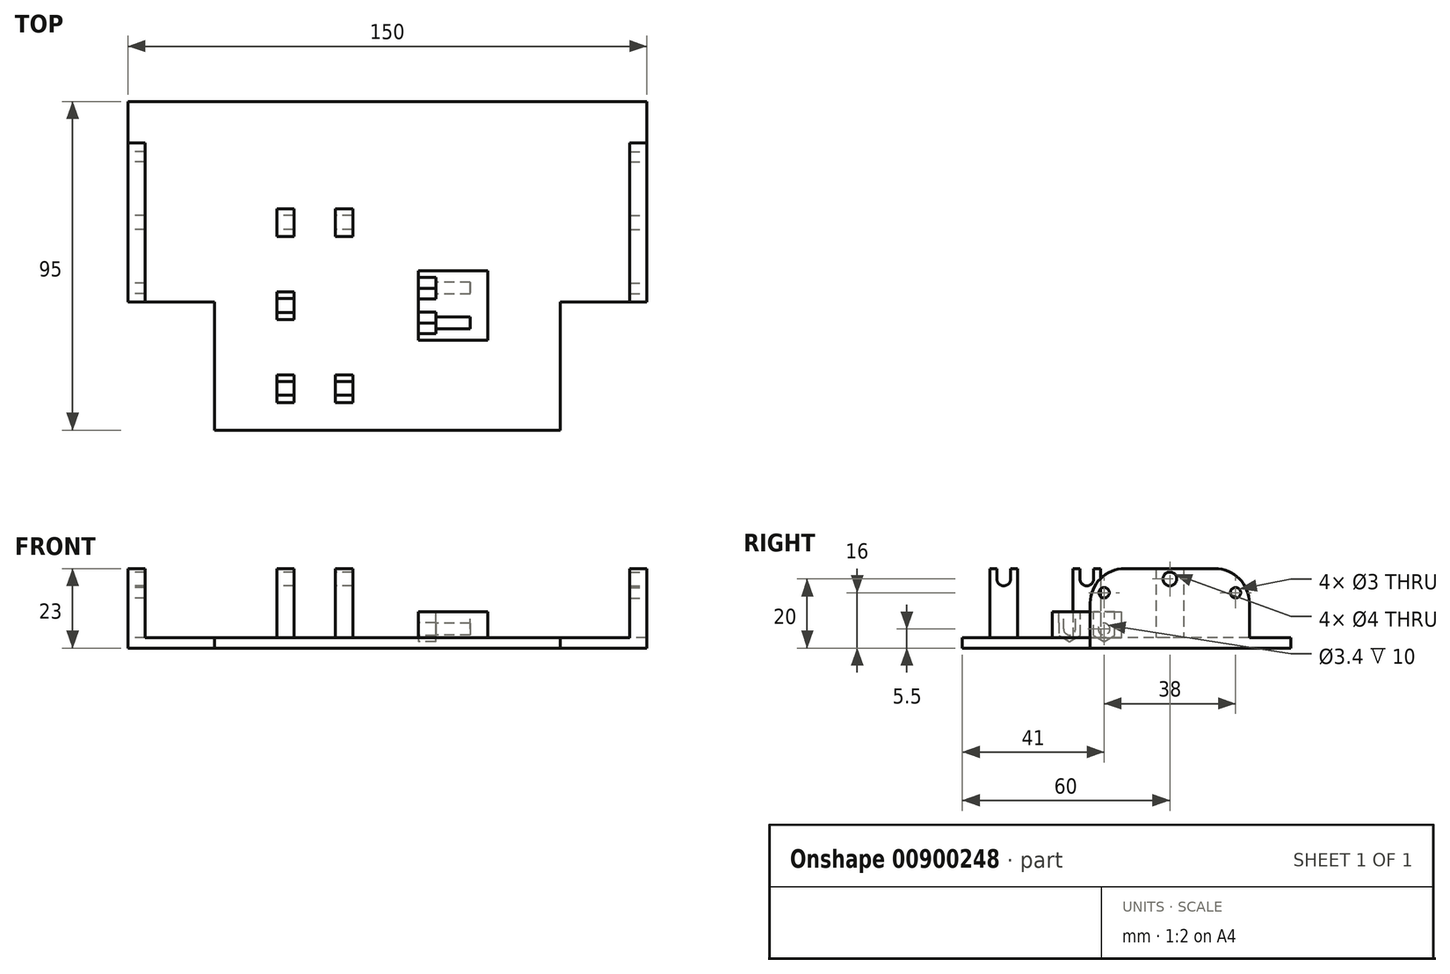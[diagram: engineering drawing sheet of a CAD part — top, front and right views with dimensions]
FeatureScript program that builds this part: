
annotation { "Feature Type Name" : "Feature", "Feature Type Description" : "" }
export const myFeature = defineFeature(function(context is Context, id is Id, definition is map)
    precondition{}
    {
        {
            var Q0;
            Q0=qCreatedBy(makeId("Top.planeOp"),FACE);
            var sketch = newSketch(context, id + "F0", { "sketchPlane" : qUnion([Q0])});
            skLineSegment(sketch, "E0.top", {"start": v(50, -18.5) * mm, "end": v(-50, -18.5) * mm});
            skLineSegment(sketch, "E0.left", {"start": v(50, 18.5) * mm, "end": v(50, -18.5) * mm});
            skLineSegment(sketch, "E0.right", {"start": v(-50, 18.5) * mm, "end": v(-50, -18.5) * mm});
            skPoint(sketch, "E0.middle", {"position": v(0, 0) * mm});
            skLineSegment(sketch, "E1.bottom", {"start": v(-75, 76.5) * mm, "end": v(75, 76.5) * mm});
            skLineSegment(sketch, "E1.top", {"start": v(-75, 18.5) * mm, "end": v(-50, 18.5) * mm});
            skLineSegment(sketch, "E1.left", {"start": v(-75, 76.5) * mm, "end": v(-75, 18.5) * mm});
            skLineSegment(sketch, "E1.right", {"start": v(75, 76.5) * mm, "end": v(75, 18.5) * mm});
            skLineSegment(sketch, "E2.trimOffspring", {"start": v(50, 18.5) * mm, "end": v(75, 18.5) * mm});
            skSolve(sketch);
        }
        {
            var Q0;
            Q0 = qSketchRegion(id + "F0", true);
            extrude(context, id + "F1", {"entities" : qUnion([Q0]), "oppositeDirection" : true, "depth" : 3 * mm, "offsetDistance" : 25.4 * mm});
        }
        {
            var Q0;
            Q0=makeQuery(id+"F1.opExtrude","SWEPT_FACE",FACE,{"disambiguationData":[OSD([sQuery(id+"F0.wireOp",EDGE,"E1.right")])]});
            var sketch = newSketch(context, id + "F2", { "sketchPlane" : qUnion([Q0])});
            skLineSegment(sketch, "E3.bottom", {"start": v(18.5, -3) * mm, "end": v(64.5, -3) * mm});
            skLineSegment(sketch, "E3.top", {"start": v(28.5, 20) * mm, "end": v(54.5, 20) * mm});
            skLineSegment(sketch, "E3.left", {"start": v(18.5, -3) * mm, "end": v(18.5, 10) * mm});
            skLineSegment(sketch, "E3.right", {"start": v(64.5, -3) * mm, "end": v(64.5, 10) * mm});
            skCircle(sketch, "E4", {"center": v(41.5, 17) * mm, "radius": 2 * mm});
            skCircle(sketch, "E5", {"center": v(22.5, 13) * mm, "radius": 1.5 * mm});
            skCircle(sketch, "E6", {"center": v(60.5, 13) * mm, "radius": 1.5 * mm});
            skPoint(sketch, "E7.visualSharp", {"position": v(18.5, 20) * mm});
            skArc(sketch, "E7.filletArc", {"start": v(28.5, 20) * mm, "mid": v(21.43, 17.07) * mm, "end": v(18.5, 10) * mm});
            skPoint(sketch, "E8.visualSharp", {"position": v(64.5, 20) * mm});
            skArc(sketch, "E8.filletArc", {"start": v(64.5, 10) * mm, "mid": v(61.57, 17.07) * mm, "end": v(54.5, 20) * mm});
            skSolve(sketch);
        }
        {
            var Q0;
            Q0 = qSketchRegion(id + "F2", true);
            extrude(context, id + "F3", {"entities" : qUnion([Q0]), "operationType" : NewBodyOperationType.ADD, "oppositeDirection" : true, "depth" : 5 * mm, "offsetDistance" : 25.4 * mm});
        }
        {
            var Q0;
            Q0=makeQuery(id+"F1.opExtrude","SWEPT_FACE",FACE,{"disambiguationData":[OSD([sQuery(id+"F0.wireOp",EDGE,"E1.left")])]});
            var sketch = newSketch(context, id + "F4", { "sketchPlane" : qUnion([Q0])});
            skLineSegment(sketch, "E9.0.0", {"start": v(-64.5, 0) * mm, "end": v(-18.5, 0) * mm});
            skLineSegment(sketch, "E9.0.1", {"start": v(-18.5, 0) * mm, "end": v(-18.5, 10) * mm});
            skArc(sketch, "E9.0.2", {"start": v(-18.5, 10) * mm, "mid": v(-21.43, 17.07) * mm, "end": v(-28.5, 20) * mm});
            skLineSegment(sketch, "E9.0.3", {"start": v(-28.5, 20) * mm, "end": v(-54.5, 20) * mm});
            skArc(sketch, "E9.0.4", {"start": v(-54.5, 20) * mm, "mid": v(-61.57, 17.07) * mm, "end": v(-64.5, 10) * mm});
            skLineSegment(sketch, "E9.0.5", {"start": v(-64.5, 10) * mm, "end": v(-64.5, 0) * mm});
            skCircle(sketch, "E10.0", {"center": v(-60.5, 13) * mm, "radius": 1.5 * mm});
            skCircle(sketch, "E11.0", {"center": v(-41.5, 17) * mm, "radius": 2 * mm});
            skCircle(sketch, "E12.0", {"center": v(-22.5, 13) * mm, "radius": 1.5 * mm});
            skSolve(sketch);
        }
        {
            var Q0;
            Q0 = qSketchRegion(id + "F4", true);
            extrude(context, id + "F5", {"entities" : qUnion([Q0]), "operationType" : NewBodyOperationType.ADD, "oppositeDirection" : true, "depth" : 5 * mm, "offsetDistance" : 25.4 * mm});
        }
        {
            var Q0;
            Q0=makeQuery(id+"F1.opExtrude","CAP_FACE",FACE,{"disambiguationData":[OSD([sQuery(id+"F0.wireOp",EDGE,"E0.top"),sQuery(id+"F0.wireOp",EDGE,"E0.left"),sQuery(id+"F0.wireOp",EDGE,"E0.right"),sQuery(id+"F0.wireOp",EDGE,"E1.bottom"),sQuery(id+"F0.wireOp",EDGE,"E1.top"),sQuery(id+"F0.wireOp",EDGE,"E1.left"),sQuery(id+"F0.wireOp",EDGE,"E1.right"),sQuery(id+"F0.wireOp",EDGE,"E2.trimOffspring")])],"isStart":true});
            var sketch = newSketch(context, id + "F6", { "sketchPlane" : qUnion([Q0])});
            skLineSegment(sketch, "E13.bottom", {"start": v(-32, 45.5) * mm, "end": v(-27, 45.5) * mm});
            skLineSegment(sketch, "E13.top", {"start": v(-32, 37.5) * mm, "end": v(-27, 37.5) * mm});
            skLineSegment(sketch, "E13.left", {"start": v(-32, 45.5) * mm, "end": v(-32, 37.5) * mm});
            skLineSegment(sketch, "E13.right", {"start": v(-27, 45.5) * mm, "end": v(-27, 37.5) * mm});
            skLineSegment(sketch, "E14.bottom", {"start": v(-32, 21.5) * mm, "end": v(-27, 21.5) * mm});
            skLineSegment(sketch, "E14.top", {"start": v(-32, 13.5) * mm, "end": v(-27, 13.5) * mm});
            skLineSegment(sketch, "E14.left", {"start": v(-32, 21.5) * mm, "end": v(-32, 13.5) * mm});
            skLineSegment(sketch, "E14.right", {"start": v(-27, 21.5) * mm, "end": v(-27, 13.5) * mm});
            skLineSegment(sketch, "E15.bottom", {"start": v(-32, -2.5) * mm, "end": v(-27, -2.5) * mm});
            skLineSegment(sketch, "E15.top", {"start": v(-32, -10.5) * mm, "end": v(-27, -10.5) * mm});
            skLineSegment(sketch, "E15.left", {"start": v(-32, -2.5) * mm, "end": v(-32, -10.5) * mm});
            skLineSegment(sketch, "E15.right", {"start": v(-27, -2.5) * mm, "end": v(-27, -10.5) * mm});
            skLineSegment(sketch, "E16.bottom", {"start": v(-15, 45.5) * mm, "end": v(-10, 45.5) * mm});
            skLineSegment(sketch, "E16.top", {"start": v(-15, 37.5) * mm, "end": v(-10, 37.5) * mm});
            skLineSegment(sketch, "E16.left", {"start": v(-15, 45.5) * mm, "end": v(-15, 37.5) * mm});
            skLineSegment(sketch, "E16.right", {"start": v(-10, 45.5) * mm, "end": v(-10, 37.5) * mm});
            skLineSegment(sketch, "E17.bottom", {"start": v(-15, -2.5) * mm, "end": v(-10, -2.5) * mm});
            skLineSegment(sketch, "E17.top", {"start": v(-15, -10.5) * mm, "end": v(-10, -10.5) * mm});
            skLineSegment(sketch, "E17.left", {"start": v(-15, -2.5) * mm, "end": v(-15, -10.5) * mm});
            skLineSegment(sketch, "E17.right", {"start": v(-10, -2.5) * mm, "end": v(-10, -10.5) * mm});
            skSolve(sketch);
        }
        {
            var Q0;
            Q0 = qSketchRegion(id + "F6", true);
            extrude(context, id + "F7", {"entities" : qUnion([Q0]), "operationType" : NewBodyOperationType.ADD, "depth" : 20 * mm, "offsetDistance" : 25.4 * mm});
        }
        {
            var Q0;
            Q0=makeQuery(id+"F7.opExtrude","SWEPT_FACE",FACE,{"disambiguationData":[OSD([sQuery(id+"F6.wireOp",EDGE,"E15.left")])]});
            var sketch = newSketch(context, id + "F8", { "sketchPlane" : qUnion([Q0])});
            skArc(sketch, "E18", {"start": v(4.5, 17) * mm, "mid": v(6.53, 15) * mm, "end": v(8.5, 17.05) * mm});
            skArc(sketch, "E19", {"start": v(-19.5, 17) * mm, "mid": v(-17.5, 15) * mm, "end": v(-15.5, 17) * mm});
            skLineSegment(sketch, "E20", {"start": v(-19.5, 17) * mm, "end": v(-19.5, 20.1) * mm});
            skLineSegment(sketch, "E21", {"start": v(-15.5, 17) * mm, "end": v(-15.5, 20.64) * mm});
            skLineSegment(sketch, "E22", {"start": v(-15.5, 20.64) * mm, "end": v(-19.5, 20.1) * mm});
            skLineSegment(sketch, "E23", {"start": v(4.5, 17) * mm, "end": v(4.48, 22.22) * mm});
            skLineSegment(sketch, "E24", {"start": v(8.5, 17.05) * mm, "end": v(8.37, 22.14) * mm});
            skLineSegment(sketch, "E25", {"start": v(8.37, 22.14) * mm, "end": v(4.48, 22.22) * mm});
            skSolve(sketch);
        }
        {
            var Q0;
            Q0 = qSketchRegion(id + "F8", true);
            extrude(context, id + "F9", {"entities" : qUnion([Q0]), "operationType" : NewBodyOperationType.REMOVE, "oppositeDirection" : true, "depth" : 25.4 * mm, "offsetDistance" : 25.4 * mm});
        }
        {
            var Q0;
            Q0=makeQuery(id+"F7.opExtrude","SWEPT_FACE",FACE,{"disambiguationData":[OSD([sQuery(id+"F6.wireOp",EDGE,"E13.left")])]});
            var sketch = newSketch(context, id + "F10", { "sketchPlane" : qUnion([Q0])});
            skCircle(sketch, "E26.0", {"center": v(-41.5, 17) * mm, "radius": 2 * mm});
            skSolve(sketch);
        }
        {
            var Q0;
            Q0 = qSketchRegion(id + "F10", true);
            extrude(context, id + "F11", {"entities" : qUnion([Q0]), "operationType" : NewBodyOperationType.REMOVE, "oppositeDirection" : true, "depth" : 25.4 * mm, "offsetDistance" : 25.4 * mm});
        }
        {
            var Q0;
            Q0=makeQuery(id+"F1.opExtrude","CAP_FACE",FACE,{"disambiguationData":[OSD([sQuery(id+"F0.wireOp",EDGE,"E0.top"),sQuery(id+"F0.wireOp",EDGE,"E0.left"),sQuery(id+"F0.wireOp",EDGE,"E0.right"),sQuery(id+"F0.wireOp",EDGE,"E1.bottom"),sQuery(id+"F0.wireOp",EDGE,"E1.top"),sQuery(id+"F0.wireOp",EDGE,"E1.left"),sQuery(id+"F0.wireOp",EDGE,"E1.right"),sQuery(id+"F0.wireOp",EDGE,"E2.trimOffspring")])],"isStart":true});
            var sketch = newSketch(context, id + "F12", { "sketchPlane" : qUnion([Q0])});
            skLineSegment(sketch, "E27.bottom", {"start": v(9, 7.5) * mm, "end": v(29, 7.5) * mm});
            skLineSegment(sketch, "E27.top", {"start": v(9, 27.5) * mm, "end": v(29, 27.5) * mm});
            skLineSegment(sketch, "E27.left", {"start": v(9, 7.5) * mm, "end": v(9, 27.5) * mm});
            skLineSegment(sketch, "E27.right", {"start": v(29, 7.5) * mm, "end": v(29, 27.5) * mm});
            skSolve(sketch);
        }
        {
            var Q0;
            Q0=makeQuery(id+"F12.imprint","IMPRINT",FACE,{"disambiguationData":[TD([[makeQuery(id+"F12.imprint","IMPRINT",EDGE,{"derivedFrom":sQuery(id+"F12.wireOp",EDGE,"E27.bottom")}),1.0]])]});
            extrude(context, id + "F13", {"entities" : qUnion([Q0]), "operationType" : NewBodyOperationType.ADD, "depth" : 7.5 * mm, "offsetDistance" : 25 * mm});
        }
        {
            var Q0;
            Q0=makeQuery(id+"F13.opExtrude","SWEPT_FACE",FACE,{"disambiguationData":[OSD([sQuery(id+"F12.wireOp",EDGE,"E27.left")])]});
            var sketch = newSketch(context, id + "F14", { "sketchPlane" : qUnion([Q0])});
            skCircle(sketch, "E28.cCircle", {"center": v(-22.5, 2.5) * mm, "radius": 3.1 * mm, "construction": true});
            skLineSegment(sketch, "E28.0", {"start": v(-19.4, 0.71) * mm, "end": v(-22.5, -1.08) * mm});
            skLineSegment(sketch, "E28.1", {"start": v(-22.5, -1.08) * mm, "end": v(-25.6, 0.71) * mm});
            skLineSegment(sketch, "E28.2", {"start": v(-25.6, 0.71) * mm, "end": v(-25.6, 4.29) * mm});
            skLineSegment(sketch, "E28.3", {"start": v(-25.6, 4.29) * mm, "end": v(-22.5, 6.08) * mm});
            skLineSegment(sketch, "E28.4", {"start": v(-22.5, 6.08) * mm, "end": v(-19.4, 4.29) * mm});
            skLineSegment(sketch, "E28.5", {"start": v(-19.4, 4.29) * mm, "end": v(-19.4, 0.71) * mm});
            skPoint(sketch, "E28.0.midPoint", {"position": v(-20.95, -0.18) * mm});
            skCircle(sketch, "E29.cCircle", {"center": v(-12.5, 2.5) * mm, "radius": 3.1 * mm, "construction": true});
            skPoint(sketch, "E29.cCircle.centerSnap0", {"position": v(-25.6, 2.5) * mm});
            skLineSegment(sketch, "E29.0", {"start": v(-9.4, 0.71) * mm, "end": v(-12.5, -1.08) * mm});
            skLineSegment(sketch, "E29.1", {"start": v(-12.5, -1.08) * mm, "end": v(-15.6, 0.71) * mm});
            skLineSegment(sketch, "E29.2", {"start": v(-15.6, 0.71) * mm, "end": v(-15.6, 4.29) * mm});
            skLineSegment(sketch, "E29.3", {"start": v(-15.6, 4.29) * mm, "end": v(-12.5, 6.08) * mm});
            skLineSegment(sketch, "E29.4", {"start": v(-12.5, 6.08) * mm, "end": v(-9.4, 4.29) * mm});
            skLineSegment(sketch, "E29.5", {"start": v(-9.4, 4.29) * mm, "end": v(-9.4, 0.71) * mm});
            skPoint(sketch, "E29.0.midPoint", {"position": v(-10.95, -0.18) * mm});
            skLineSegment(sketch, "E30", {"start": v(-17.5, -2.38) * mm, "end": v(-17.5, 12.1) * mm, "construction": true});
            skCircle(sketch, "E31", {"center": v(-22.5, 2.5) * mm, "radius": 1.7 * mm});
            skCircle(sketch, "E32", {"center": v(-12.5, 2.5) * mm, "radius": 1.7 * mm});
            skLineSegment(sketch, "E33.bottom", {"start": v(-25.6, 4.29) * mm, "end": v(-19.4, 4.29) * mm});
            skLineSegment(sketch, "E33.top", {"start": v(-25.6, 10.64) * mm, "end": v(-19.4, 10.64) * mm});
            skLineSegment(sketch, "E33.left", {"start": v(-25.6, 4.29) * mm, "end": v(-25.6, 10.64) * mm});
            skLineSegment(sketch, "E33.right", {"start": v(-19.4, 4.29) * mm, "end": v(-19.4, 10.64) * mm});
            skLineSegment(sketch, "E34.bottom", {"start": v(-15.6, 4.29) * mm, "end": v(-9.38, 4.29) * mm});
            skLineSegment(sketch, "E34.top", {"start": v(-15.6, 11.52) * mm, "end": v(-9.38, 11.52) * mm});
            skLineSegment(sketch, "E34.left", {"start": v(-15.6, 4.29) * mm, "end": v(-15.6, 11.52) * mm});
            skLineSegment(sketch, "E35", {"start": v(-9.38, 4.29) * mm, "end": v(-9.38, 11.52) * mm});
            skSolve(sketch);
        }
        {
            var Q0;
            Q0 = qSketchRegion(id + "F14", true);
            var Q1;
            Q1=makeQuery(id+"F14.imprint","IMPRINT",FACE,{"disambiguationData":[TD([[makeQuery(id+"F14.imprint","IMPRINT",EDGE,{"derivedFrom":sQuery(id+"F14.wireOp",EDGE,"E31")}),1.0]])]});
            var Q2;
            Q2=makeQuery(id+"F14.imprint","IMPRINT",FACE,{"disambiguationData":[TD([[makeQuery(id+"F14.imprint","IMPRINT",EDGE,{"derivedFrom":sQuery(id+"F14.wireOp",EDGE,"E32")}),1.0]])]});
            extrude(context, id + "F15", {"entities" : qUnion([Q0, Q1, Q2]), "operationType" : NewBodyOperationType.REMOVE, "oppositeDirection" : true, "depth" : 5 * mm, "offsetDistance" : 25 * mm});
        }
        {
            var Q0;
            Q0=makeQuery(id+"F14.imprint","IMPRINT",FACE,{"disambiguationData":[TD([[makeQuery(id+"F14.imprint","IMPRINT",EDGE,{"derivedFrom":sQuery(id+"F14.wireOp",EDGE,"E31")}),1.0]])]});
            var Q1;
            Q1=makeQuery(id+"F14.imprint","IMPRINT",FACE,{"disambiguationData":[TD([[makeQuery(id+"F14.imprint","IMPRINT",EDGE,{"derivedFrom":sQuery(id+"F14.wireOp",EDGE,"E32")}),1.0]])]});
            extrude(context, id + "F16", {"entities" : qUnion([Q0, Q1]), "operationType" : NewBodyOperationType.REMOVE, "oppositeDirection" : true, "depth" : 15 * mm, "offsetDistance" : 25 * mm});
        }
        {
            var Q0;
            Q0=makeQuery(id+"F15.boolean.opBoolean","COPY",FACE,{"derivedFrom":makeQuery(id+"F15.opExtrude","CAP_FACE",FACE,{"disambiguationData":[OSD([sQuery(id+"F14.wireOp",EDGE,"E29.0"),sQuery(id+"F14.wireOp",EDGE,"E29.1"),sQuery(id+"F14.wireOp",EDGE,"E29.2"),sQuery(id+"F14.wireOp",EDGE,"E29.5"),sQuery(id+"F14.wireOp",EDGE,"E34.bottom"),sQuery(id+"F14.wireOp",EDGE,"E34.top"),sQuery(id+"F14.wireOp",EDGE,"E34.left"),sQuery(id+"F14.wireOp",EDGE,"E35")])],"isStart":false})});
            var sketch = newSketch(context, id + "F17", { "sketchPlane" : qUnion([Q0])});
            skLineSegment(sketch, "E36.bottom", {"start": v(-14.2, 2.5) * mm, "end": v(-10.8, 2.5) * mm});
            skLineSegment(sketch, "E36.top", {"start": v(-14.2, 8.48) * mm, "end": v(-10.8, 8.48) * mm});
            skLineSegment(sketch, "E36.left", {"start": v(-14.2, 2.5) * mm, "end": v(-14.2, 8.48) * mm});
            skLineSegment(sketch, "E36.right", {"start": v(-10.8, 2.5) * mm, "end": v(-10.8, 8.48) * mm});
            skSolve(sketch);
        }
        {
            var Q0;
            {var subQ0=sQuery(id+"F17.wireOp",EDGE,"E36.left");var subQ1=sQuery(id+"F17.wireOp",EDGE,"E36.bottom");var subQ2=makeQuery(id+"F15.opExtrude","CAP_FACE",FACE,{"disambiguationData":[OSD([sQuery(id+"F14.wireOp",EDGE,"E29.0"),sQuery(id+"F14.wireOp",EDGE,"E29.1"),sQuery(id+"F14.wireOp",EDGE,"E29.2"),sQuery(id+"F14.wireOp",EDGE,"E29.5"),sQuery(id+"F14.wireOp",EDGE,"E34.bottom"),sQuery(id+"F14.wireOp",EDGE,"E34.top"),sQuery(id+"F14.wireOp",EDGE,"E34.left"),sQuery(id+"F14.wireOp",EDGE,"E35")])],"isStart":false});var subQ3=makeQuery(id+"F16.boolean.opBoolean","INTERSECT",EDGE,{"derivedFrom":[makeQuery(id+"F15.boolean.opBoolean","COPY",FACE,{"derivedFrom":subQ2}),makeQuery(id+"F16.opExtrude","SWEPT_FACE",FACE,{"disambiguationData":[OSD([sQuery(id+"F14.wireOp",EDGE,"E32")])]})]});var subQ4=makeQuery(id+"F17.imprint","INTERSECT",VERTEX,{"derivedFrom":[subQ3,subQ1,subQ0]});Q0=makeQuery(id+"F17.imprint","IMPRINT",FACE,{"disambiguationData":[TD([[makeQuery(id+"F17.imprint","IMPRINT",EDGE,{"disambiguationData":[TD([[subQ4,-1.0]])],"derivedFrom":subQ0}),-1.0]])]});}
            extrude(context, id + "F18", {"entities" : qUnion([Q0]), "operationType" : NewBodyOperationType.REMOVE, "oppositeDirection" : true, "depth" : 10 * mm, "offsetDistance" : 25 * mm});
        }
    });
